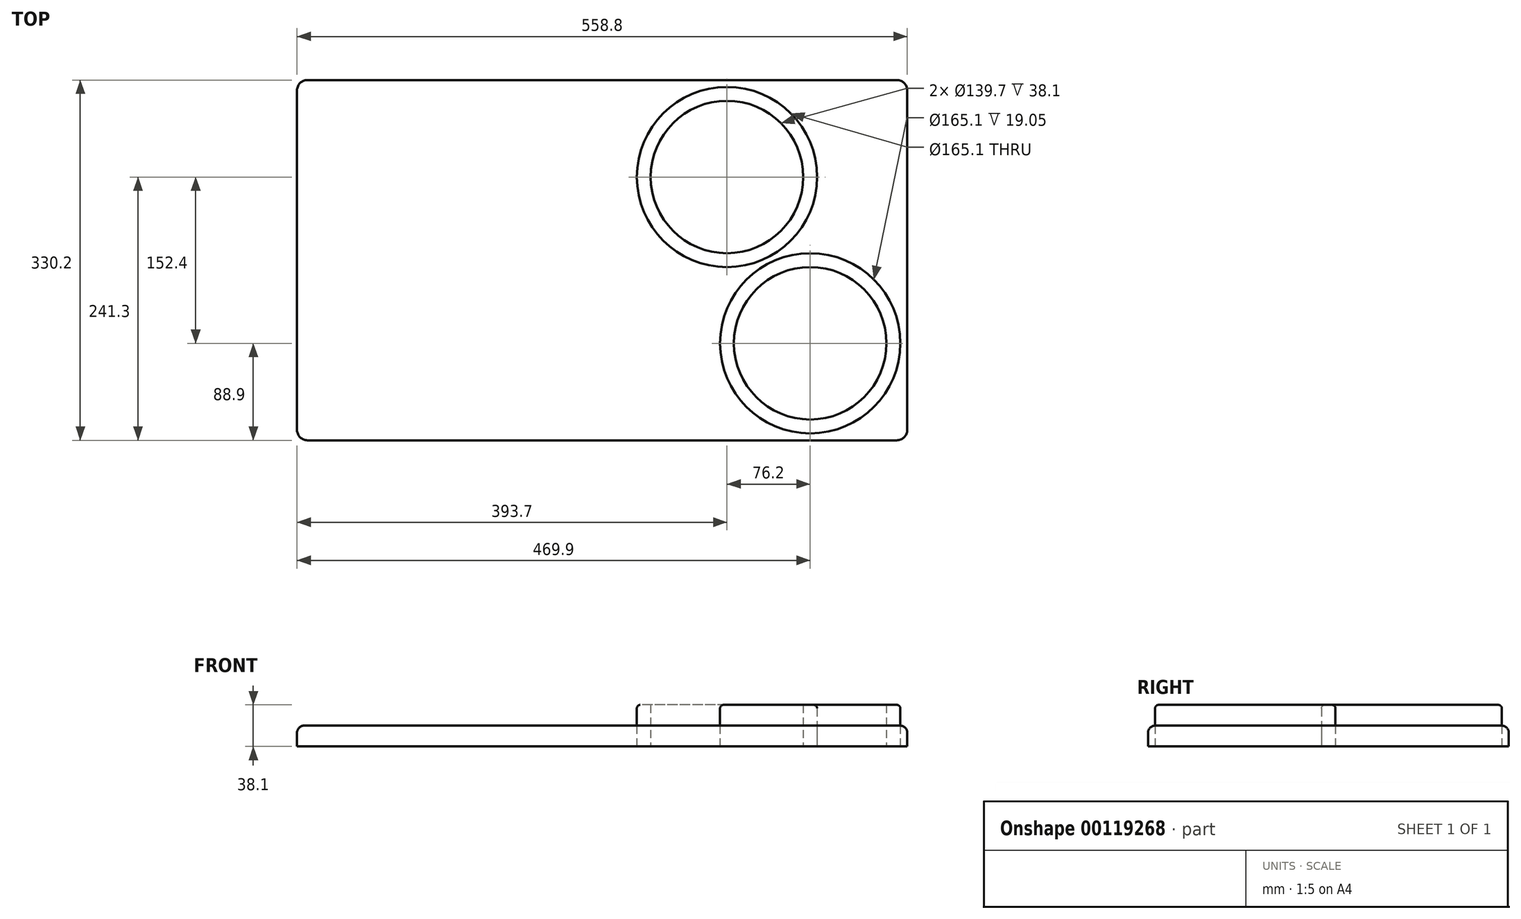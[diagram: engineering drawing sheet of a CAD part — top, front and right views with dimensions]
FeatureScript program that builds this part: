
annotation { "Feature Type Name" : "Feature", "Feature Type Description" : "" }
export const myFeature = defineFeature(function(context is Context, id is Id, definition is map)
    precondition{}
    {
        {
            var Q0;
            Q0=qCreatedBy(makeId("Top.planeOp"),FACE);
            var sketch = newSketch(context, id + "F0", { "sketchPlane" : qUnion([Q0])});
            skLineSegment(sketch, "E0.bottom", {"start": v(0, 0) * mm, "end": v(558.8, 0) * mm});
            skLineSegment(sketch, "E0.top", {"start": v(0, 330.2) * mm, "end": v(558.8, 330.2) * mm});
            skLineSegment(sketch, "E0.left", {"start": v(0, 0) * mm, "end": v(0, 330.2) * mm});
            skLineSegment(sketch, "E0.right", {"start": v(558.8, 0) * mm, "end": v(558.8, 330.2) * mm});
            skCircle(sketch, "E1", {"center": v(469.9, 88.9) * mm, "radius": 82.55 * mm});
            skCircle(sketch, "E2", {"center": v(393.7, 241.3) * mm, "radius": 82.55 * mm});
            skCircle(sketch, "E3", {"center": v(469.9, 88.9) * mm, "radius": 69.85 * mm});
            skCircle(sketch, "E4", {"center": v(393.7, 241.3) * mm, "radius": 69.85 * mm});
            skSolve(sketch);
        }
        {
            var Q0;
            Q0=makeQuery(id+"F0.imprint","IMPRINT",FACE,{"disambiguationData":[TD([[makeQuery(id+"F0.imprint","IMPRINT",EDGE,{"derivedFrom":sQuery(id+"F0.wireOp",EDGE,"E2")}),1.0]])]});
            var Q1;
            Q1=makeQuery(id+"F0.imprint","IMPRINT",FACE,{"disambiguationData":[TD([[makeQuery(id+"F0.imprint","IMPRINT",EDGE,{"derivedFrom":sQuery(id+"F0.wireOp",EDGE,"E1")}),1.0]])]});
            extrude(context, id + "F1", {"entities" : qUnion([Q0, Q1]), "depth" : 38.1 * mm});
        }
        {
            var Q0;
            Q0=makeQuery(id+"F0.imprint","IMPRINT",FACE,{"disambiguationData":[TD([[makeQuery(id+"F0.imprint","IMPRINT",EDGE,{"derivedFrom":sQuery(id+"F0.wireOp",EDGE,"E0.bottom")}),1.0]])]});
            extrude(context, id + "F2", {"entities" : qUnion([Q0]), "depth" : 19.05 * mm});
        }
        {
            var Q0;
            Q0=makeQuery(id+"F2.opExtrude","CAP_EDGE",EDGE,{"disambiguationData":[OSD([sQuery(id+"F0.wireOp",EDGE,"E0.left")])],"isStart":false});
            var Q1;
            Q1=makeQuery(id+"F2.opExtrude","CAP_EDGE",EDGE,{"disambiguationData":[OSD([sQuery(id+"F0.wireOp",EDGE,"E0.top")])],"isStart":false});
            var Q2;
            Q2=makeQuery(id+"F2.opExtrude","CAP_EDGE",EDGE,{"disambiguationData":[OSD([sQuery(id+"F0.wireOp",EDGE,"E0.bottom")])],"isStart":false});
            var Q3;
            Q3=makeQuery(id+"F2.opExtrude","CAP_EDGE",EDGE,{"disambiguationData":[OSD([sQuery(id+"F0.wireOp",EDGE,"E0.right")])],"isStart":false});
            fillet(context, id + "F3", {"entities" : qUnion([Q0, Q1, Q2, Q3]), "radius" : 6.35 * mm, "tangentPropagation" : true, "allowEdgeOverflow" : false});
        }
        {
            var Q0;
            Q0=makeQuery(id+"F2.opExtrude","SWEPT_EDGE",EDGE,{"disambiguationData":[OSD([sQuery(id+"F0.wireOp",EDGE,"E0.bottom"),sQuery(id+"F0.wireOp",EDGE,"E0.left")])]});
            var Q1;
            Q1=makeQuery(id+"F2.opExtrude","SWEPT_EDGE",EDGE,{"disambiguationData":[OSD([sQuery(id+"F0.wireOp",EDGE,"E0.bottom"),sQuery(id+"F0.wireOp",EDGE,"E0.right")])]});
            var Q2;
            Q2=makeQuery(id+"F2.opExtrude","SWEPT_EDGE",EDGE,{"disambiguationData":[OSD([sQuery(id+"F0.wireOp",EDGE,"E0.top"),sQuery(id+"F0.wireOp",EDGE,"E0.right")])]});
            var Q3;
            Q3=makeQuery(id+"F2.opExtrude","SWEPT_EDGE",EDGE,{"disambiguationData":[OSD([sQuery(id+"F0.wireOp",EDGE,"E0.top"),sQuery(id+"F0.wireOp",EDGE,"E0.left")])]});
            fillet(context, id + "F4", {"entities" : qUnion([Q0, Q1, Q2, Q3]), "radius" : 9.52 * mm, "tangentPropagation" : true, "allowEdgeOverflow" : false});
        }
        {
            var Q0;
            Q0=makeQuery(id+"F1.opExtrude","CAP_EDGE",EDGE,{"disambiguationData":[OSD([sQuery(id+"F0.wireOp",EDGE,"E1")])],"isStart":false});
            var Q1;
            Q1=makeQuery(id+"F1.opExtrude","CAP_EDGE",EDGE,{"disambiguationData":[OSD([sQuery(id+"F0.wireOp",EDGE,"E2")])],"isStart":false});
            fillet(context, id + "F5", {"entities" : qUnion([Q0, Q1]), "radius" : 3.17 * mm, "tangentPropagation" : true, "allowEdgeOverflow" : false});
        }
    });
